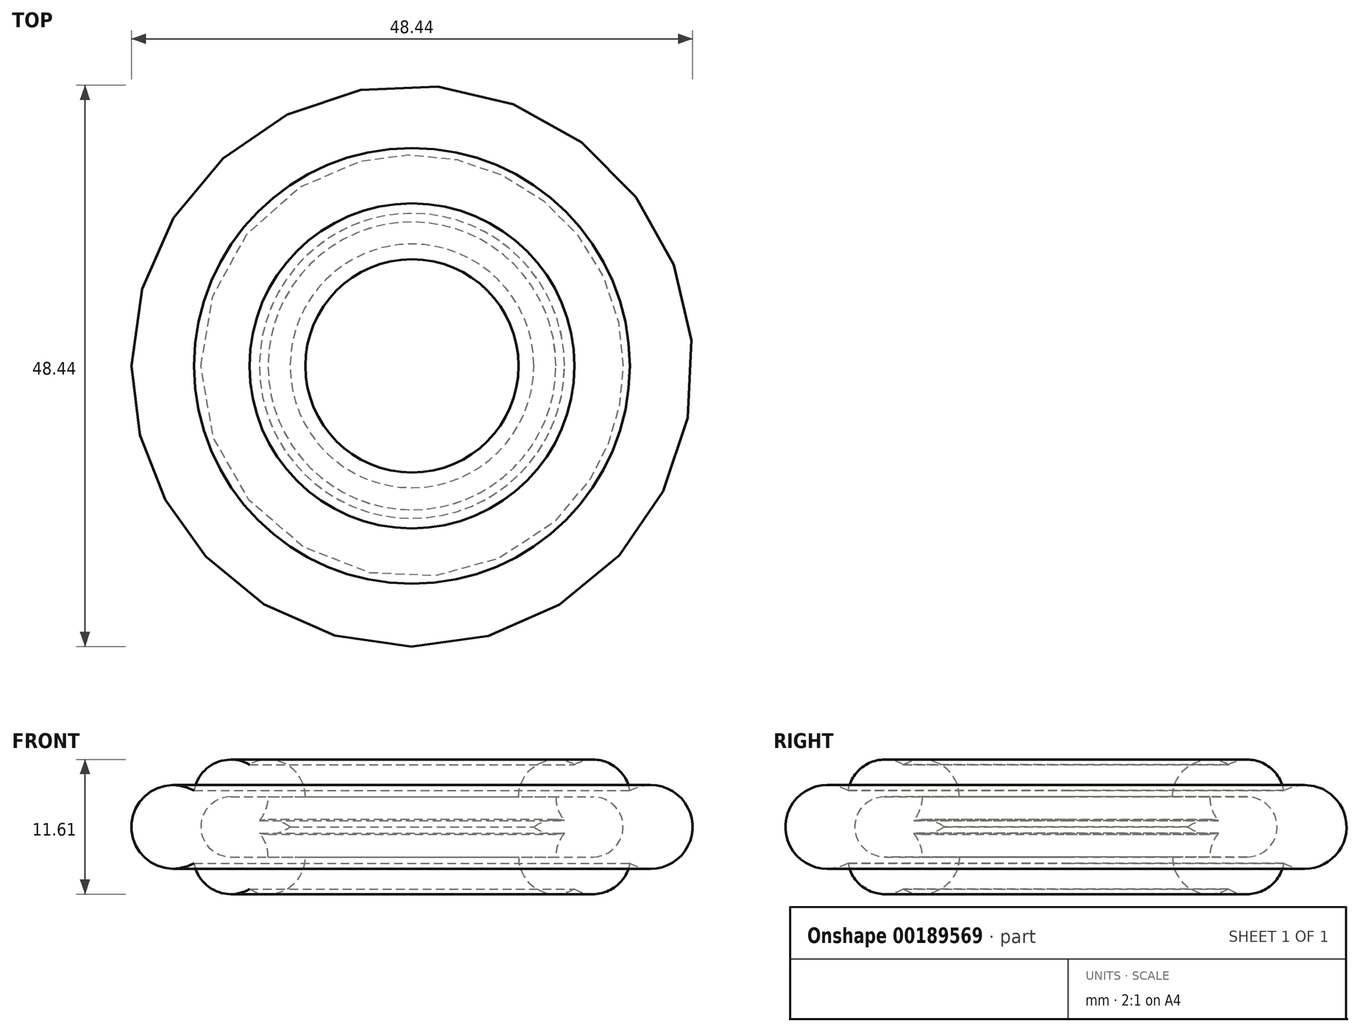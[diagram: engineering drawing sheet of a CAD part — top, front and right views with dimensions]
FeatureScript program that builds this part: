
annotation { "Feature Type Name" : "Feature", "Feature Type Description" : "" }
export const myFeature = defineFeature(function(context is Context, id is Id, definition is map)
    precondition{}
    {
        {
            var Q0;
            Q0=qCreatedBy(makeId("Front.planeOp"),FACE);
            var sketch = newSketch(context, id + "F0", { "sketchPlane" : qUnion([Q0])});
            skLineSegment(sketch, "E0.bottom", {"start": v(0, 0) * mm, "end": v(-15.63, 0) * mm});
            skLineSegment(sketch, "E0.top", {"start": v(0, 5.18) * mm, "end": v(-15.63, 5.18) * mm});
            skLineSegment(sketch, "E0.left", {"start": v(0, 0) * mm, "end": v(0, 5.18) * mm});
            skLineSegment(sketch, "E0.right", {"start": v(-15.63, 0) * mm, "end": v(-15.63, 5.18) * mm});
            skPoint(sketch, "E1.centerSnap0", {"position": v(-15.63, 2.6) * mm});
            skPoint(sketch, "E1.center.orphan", {"position": v(-20.6, 2.6) * mm});
            skArc(sketch, "E2", {"start": v(-15.63, 5.18) * mm, "mid": v(-18.22, 2.6) * mm, "end": v(-15.63, 0) * mm});
            skCircle(sketch, "E3", {"center": v(-15.63, 5.18) * mm, "radius": 3.21 * mm});
            skCircle(sketch, "E4", {"center": v(-15.63, 0) * mm, "radius": 3.21 * mm});
            skCircle(sketch, "E5", {"center": v(-12.42, 5.18) * mm, "radius": 3.21 * mm});
            skCircle(sketch, "E6", {"center": v(-12.42, 0) * mm, "radius": 3.21 * mm});
            skCircle(sketch, "E7", {"center": v(-20.6, 2.6) * mm, "radius": 3.61 * mm});
            skSolve(sketch);
        }
        {
            var Q0;
            Q0 = qSketchRegion(id + "F0", true);
            var Q1;
            Q1=sQuery(id+"F0.wireOp",EDGE,"E0.left");
            revolve(context, id + "F1", {"entities" : qUnion([Q0]), "axis" : qUnion([Q1]), "revolveType" : RevolveType.FULL});
        }
    });
